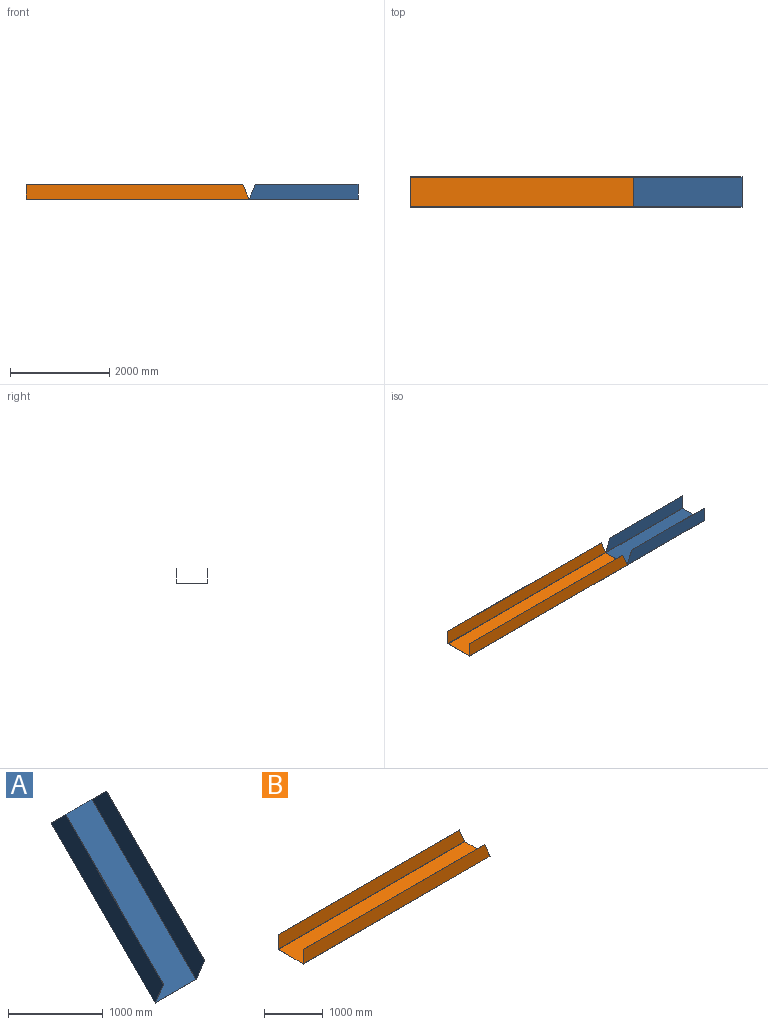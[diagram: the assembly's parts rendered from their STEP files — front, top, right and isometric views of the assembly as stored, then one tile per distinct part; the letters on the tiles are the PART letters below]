
ASSEMBLY  parts=2 mates=1
PART A: 22 faces, bbox 616.4x1681.2x1770.5 mm
  f0: plane 602.74x2.42mm, normal (0,-0.71,-0.71), area 2059.1mm2, adj f2,f3,f10,f19
  f1: plane 602.74x2.42mm, normal (0,0.71,0.71), area 2059.1mm2, adj f2,f3,f9,f18
  f2: plane 1552.53x1552.53mm, normal (0,0.71,-0.71), area 1323381.4mm2, adj f0,f1,f11,f20
  f3: plane 1552.53x1552.53mm, normal (0,-0.71,0.71), area 1323381.4mm2, adj f0,f1,f12,f21
  f4: plane 1463.25x1463.25mm, normal (0,-0.71,0.71), area 7069.5mm2, adj f5,f6,f7,f8
  f5: plane 213.1x213.1mm, normal (0,0.71,0.71), area 1029.6mm2, adj f4,f7,f8,f9
  f6: plane 301.37x124.83mm, normal (0,-0.92,-0.38), area 1114.4mm2, adj f4,f7,f8,f10
  f7: plane 1764.62x1676.35mm, normal (-1,0,0), area 642452.3mm2, adj f4,f5,f6,f11
  f8: plane 1764.62x1676.35mm, normal (1,0,0), area 642452.3mm2, adj f4,f5,f6,f12
  f9: plane 6.85x4.84mm, normal (0,0.71,0.71), area 27.6mm2, adj f1,f5,f11,f12
  f10: bspline ~6.85x5.84mm, area 28.1mm2, adj f0,f6,f11,f12
  f11: cylinder r=6.85mm len=1557.37mm, axis (0,0.71,0.71), area 23600.7mm2, adj f2,f7,f9,f10
  f12: cylinder r=3.43mm len=1554.95mm, axis (0,0.71,0.71), area 11822.3mm2, adj f3,f8,f9,f10
  f13: plane 1463.25x1463.25mm, normal (0,-0.71,0.71), area 7069.5mm2, adj f14,f15,f16,f17
  f14: plane 301.37x124.83mm, normal (0,-0.92,-0.38), area 1114.4mm2, adj f13,f16,f17,f19
  f15: plane 213.1x213.1mm, normal (0,0.71,0.71), area 1029.6mm2, adj f13,f16,f17,f18
  f16: plane 1764.62x1676.35mm, normal (1,0,0), area 642452.3mm2, adj f13,f14,f15,f20
  f17: plane 1764.62x1676.35mm, normal (-1,0,0), area 642452.3mm2, adj f13,f14,f15,f21
  f18: plane 6.85x4.84mm, normal (0,0.71,0.71), area 27.6mm2, adj f1,f15,f20,f21
  f19: bspline ~6.85x5.84mm, area 28.2mm2, adj f0,f14,f20,f21
  f20: cylinder r=6.85mm len=1557.37mm, axis (0,0.71,0.71), area 23600.7mm2, adj f2,f16,f18,f19
  f21: cylinder r=3.43mm len=1554.95mm, axis (0,0.71,0.71), area 11822.3mm2, adj f3,f17,f18,f19
PART B: 22 faces, bbox 4500x616.4x308.2 mm
  f0: plane 301.37x3.42mm, normal (-1,0,0), area 1029.6mm2, adj f1,f3,f4,f14
  f1: plane 4373.75x3.42mm, normal (0,0,1), area 14942mm2, adj f0,f2,f3,f4
  f2: plane 301.37x124.83mm, normal (0.92,0,0.38), area 1114.4mm2, adj f1,f3,f4,f15
  f3: plane 4498.58x301.37mm, normal (0,1,0), area 1336931.1mm2, adj f0,f1,f2,f16
  f4: plane 4498.58x301.37mm, normal (0,-1,0), area 1336931.1mm2, adj f0,f1,f2,f17
  f5: plane 301.37x124.83mm, normal (0.92,0,0.38), area 1114.4mm2, adj f6,f8,f9,f19
  f6: plane 4373.75x3.42mm, normal (0,0,1), area 14942mm2, adj f5,f7,f8,f9
  f7: plane 301.37x3.42mm, normal (-1,0,0), area 1029.6mm2, adj f6,f8,f9,f18
  f8: plane 4498.58x301.37mm, normal (0,-1,0), area 1336931.1mm2, adj f5,f6,f7,f20
  f9: plane 4498.58x301.37mm, normal (0,1,0), area 1336931.1mm2, adj f5,f6,f7,f21
  f10: plane 602.74x3.42mm, normal (-1,0,0), area 2059.1mm2, adj f12,f13,f14,f18
  f11: plane 602.74x3.42mm, normal (1,0,0), area 2059.1mm2, adj f12,f13,f15,f19
  f12: plane 4500x602.74mm, normal (0,0,-1), area 2712339mm2, adj f10,f11,f16,f20
  f13: plane 4500x602.74mm, normal (0,0,1), area 2712339mm2, adj f10,f11,f17,f21
  f14: plane 6.85x6.85mm, normal (-1,0,0), area 27.6mm2, adj f0,f10,f16,f17
  f15: bspline ~6.85x6.85mm, area 28.2mm2, adj f2,f11,f16,f17
  f16: cylinder r=6.85mm len=4500mm, axis (-1,0,0), area 48378.9mm2, adj f3,f12,f14,f15
  f17: cylinder r=3.43mm len=4500mm, axis (-1,0,0), area 24234.3mm2, adj f4,f13,f14,f15
  f18: plane 6.85x6.85mm, normal (-1,0,0), area 27.6mm2, adj f7,f10,f20,f21
  f19: bspline ~6.85x6.85mm, area 28.1mm2, adj f5,f11,f20,f21
  f20: cylinder r=6.85mm len=4500mm, axis (-1,0,0), area 48378.9mm2, adj f8,f12,f18,f19
  f21: cylinder r=3.43mm len=4500mm, axis (-1,0,0), area 24234.3mm2, adj f9,f13,f18,f19
PLACE A rot(axis=(-0.36,0.36,-0.86),98.4deg) t=(126.25,0,0)mm
PLACE B at identity
MATE parallel A.f0 <-> B.f11  axis (-1,0,0) through (63.13,0,-154.11)mm
